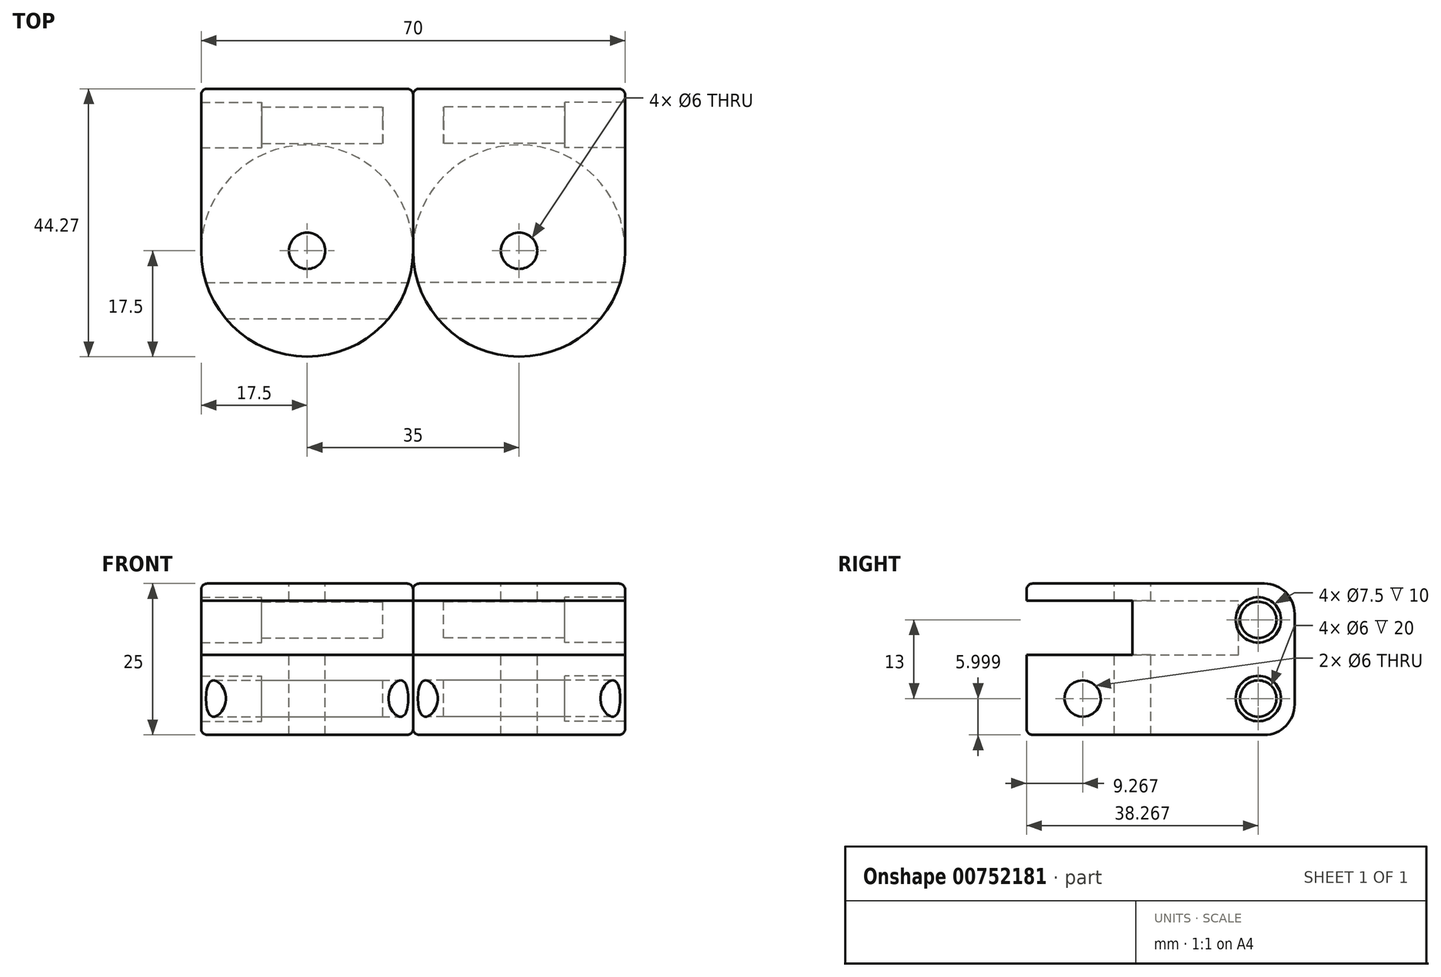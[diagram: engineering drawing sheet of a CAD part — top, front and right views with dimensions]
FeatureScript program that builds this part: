
annotation { "Feature Type Name" : "Feature", "Feature Type Description" : "" }
export const myFeature = defineFeature(function(context is Context, id is Id, definition is map)
    precondition{}
    {
        {
            var Q0;
            Q0=qCreatedBy(makeId("Right.planeOp"),FACE);
            var sketch = newSketch(context, id + "F0", { "sketchPlane" : qUnion([Q0])});
            skLineSegment(sketch, "E0.bottom", {"start": v(-22.23, 10.8) * mm, "end": v(17.77, 10.8) * mm});
            skLineSegment(sketch, "E0.top", {"start": v(-22.23, -14.2) * mm, "end": v(17.77, -14.2) * mm});
            skLineSegment(sketch, "E0.left", {"start": v(-22.23, 10.8) * mm, "end": v(-22.23, -14.2) * mm});
            skLineSegment(sketch, "E0.right", {"start": v(22.77, 5.8) * mm, "end": v(22.77, -9.2) * mm});
            skCircle(sketch, "E1", {"center": v(16.77, 4.8) * mm, "radius": 3 * mm});
            skCircle(sketch, "E2", {"center": v(16.77, -8.2) * mm, "radius": 3 * mm});
            skPoint(sketch, "E3.visualSharp", {"position": v(22.77, 10.8) * mm});
            skArc(sketch, "E3.filletArc", {"start": v(22.77, 5.8) * mm, "mid": v(21.3, 9.33) * mm, "end": v(17.77, 10.8) * mm});
            skPoint(sketch, "E4.visualSharp", {"position": v(22.77, -14.2) * mm});
            skArc(sketch, "E4.filletArc", {"start": v(17.77, -14.2) * mm, "mid": v(21.3, -12.74) * mm, "end": v(22.77, -9.2) * mm});
            skCircle(sketch, "E5", {"center": v(16.77, 4.8) * mm, "radius": 3.75 * mm});
            skCircle(sketch, "E6", {"center": v(16.77, -8.2) * mm, "radius": 3.75 * mm});
            skCircle(sketch, "E7", {"center": v(-12.23, -8.2) * mm, "radius": 3 * mm});
            skSolve(sketch);
        }
        {
            var Q0;
            Q0=makeQuery(id+"F0.imprint","IMPRINT",FACE,{"disambiguationData":[TD([[makeQuery(id+"F0.imprint","IMPRINT",EDGE,{"derivedFrom":sQuery(id+"F0.wireOp",EDGE,"E0.bottom")}),-1.0]])]});
            extrude(context, id + "F1", {"entities" : qUnion([Q0]), "depth" : 35 * mm, "offsetDistance" : 25 * mm});
        }
        {
            var Q0;
            Q0=makeQuery(id+"F0.imprint","IMPRINT",FACE,{"disambiguationData":[TD([[makeQuery(id+"F0.imprint","IMPRINT",EDGE,{"derivedFrom":sQuery(id+"F0.wireOp",EDGE,"E1")}),-1.0]])]});
            var Q1;
            Q1=makeQuery(id+"F0.imprint","IMPRINT",FACE,{"disambiguationData":[TD([[makeQuery(id+"F0.imprint","IMPRINT",EDGE,{"derivedFrom":sQuery(id+"F0.wireOp",EDGE,"E2")}),-1.0]])]});
            extrude(context, id + "F2", {"entities" : qUnion([Q0, Q1]), "operationType" : NewBodyOperationType.ADD, "depth" : 25 * mm, "offsetDistance" : 25 * mm});
        }
        {
            var Q0;
            Q0=makeQuery(id+"F0.imprint","IMPRINT",FACE,{"disambiguationData":[TD([[makeQuery(id+"F0.imprint","IMPRINT",EDGE,{"derivedFrom":sQuery(id+"F0.wireOp",EDGE,"E1")}),1.0]])]});
            var Q1;
            Q1=makeQuery(id+"F0.imprint","IMPRINT",FACE,{"disambiguationData":[TD([[makeQuery(id+"F0.imprint","IMPRINT",EDGE,{"derivedFrom":sQuery(id+"F0.wireOp",EDGE,"E2")}),1.0]])]});
            extrude(context, id + "F3", {"entities" : qUnion([Q0, Q1]), "operationType" : NewBodyOperationType.ADD, "depth" : 5 * mm, "offsetDistance" : 25 * mm});
        }
        {
            var Q0;
            Q0=qCreatedBy(makeId("Top.planeOp"),FACE);
            var sketch = newSketch(context, id + "F4", { "sketchPlane" : qUnion([Q0])});
            skCircle(sketch, "E8", {"center": v(17.5, -4) * mm, "radius": 15 * mm});
            skCircle(sketch, "E9", {"center": v(17.5, -4) * mm, "radius": 17.5 * mm});
            skLineSegment(sketch, "E10", {"start": v(0, 0) * mm, "end": v(0, -24.2) * mm});
            skLineSegment(sketch, "E11", {"start": v(0, -24.2) * mm, "end": v(35, -24.2) * mm});
            skLineSegment(sketch, "E12", {"start": v(35, -24.2) * mm, "end": v(35, 0) * mm});
            skSolve(sketch);
        }
        {
            var Q0;
            {var subQ0=sQuery(id+"F4.wireOp",EDGE,"E10");Q0=makeQuery(id+"F4.imprint","IMPRINT",FACE,{"disambiguationData":[TD([[makeQuery(id+"F4.imprint","IMPRINT",EDGE,{"derivedFrom":subQ0}),1.0]])]});}
            extrude(context, id + "F5", {"entities" : qUnion([Q0]), "operationType" : NewBodyOperationType.REMOVE, "oppositeDirection" : true, "depth" : 25 * mm, "offsetDistance" : 25 * mm, "hasSecondDirection" : true, "secondDirectionOppositeDirection" : false, "secondDirectionDepth" : 25 * mm});
        }
        {
            var Q0;
            Q0=makeQuery(id+"F4.imprint","IMPRINT",FACE,{"disambiguationData":[TD([[makeQuery(id+"F4.imprint","IMPRINT",EDGE,{"derivedFrom":sQuery(id+"F4.wireOp",EDGE,"E8")}),-1.0]])]});
            var Q1;
            Q1=makeQuery(id+"F4.imprint","IMPRINT",FACE,{"disambiguationData":[TD([[makeQuery(id+"F4.imprint","IMPRINT",EDGE,{"derivedFrom":sQuery(id+"F4.wireOp",EDGE,"E8")}),1.0]])]});
            extrude(context, id + "F6", {"entities" : qUnion([Q0, Q1]), "operationType" : NewBodyOperationType.REMOVE, "oppositeDirection" : true, "depth" : 1 * mm, "offsetDistance" : 25 * mm, "hasSecondDirection" : true, "secondDirectionOppositeDirection" : false, "secondDirectionDepth" : 8 * mm});
        }
        {
            var Q0;
            Q0=qCreatedBy(makeId("Top.planeOp"),FACE);
            var sketch = newSketch(context, id + "F7", { "sketchPlane" : qUnion([Q0])});
            skCircle(sketch, "E13", {"center": v(17.5, -4) * mm, "radius": 3 * mm});
            skSolve(sketch);
        }
        {
            var Q0;
            Q0=qSketchRegion(id+"F7",true);
            extrude(context, id + "F8", {"entities" : qUnion([Q0]), "operationType" : NewBodyOperationType.REMOVE, "oppositeDirection" : true, "depth" : 25 * mm, "offsetDistance" : 25 * mm, "hasSecondDirection" : true, "secondDirectionOppositeDirection" : false, "secondDirectionDepth" : 25 * mm});
        }
        {
            var Q0;
            Q0=makeQuery(id+"F5.boolean.opBoolean","INTERSECT",EDGE,{"derivedFrom":[makeQuery(id+"F1.opExtrude","SWEPT_FACE",FACE,{"disambiguationData":[OSD([sQuery(id+"F0.wireOp",EDGE,"E0.top")])]}),makeQuery(id+"F5.opExtrude","SWEPT_FACE",FACE,{"disambiguationData":[OSD([sQuery(id+"F4.wireOp",EDGE,"E9")])]})]});
            var Q1;
            Q1=makeQuery(id+"F1.opExtrude","CAP_EDGE",EDGE,{"disambiguationData":[OSD([sQuery(id+"F0.wireOp",EDGE,"E0.top")])],"isStart":true});
            var Q2;
            Q2=makeQuery(id+"F1.opExtrude","CAP_EDGE",EDGE,{"disambiguationData":[OSD([sQuery(id+"F0.wireOp",EDGE,"E0.top")])],"isStart":false});
            var Q3;
            Q3=makeQuery(id+"F1.opExtrude","CAP_EDGE",EDGE,{"disambiguationData":[OSD([sQuery(id+"F0.wireOp",EDGE,"E4.filletArc")])],"isStart":true});
            var Q4;
            Q4=makeQuery(id+"F1.opExtrude","CAP_EDGE",EDGE,{"disambiguationData":[OSD([sQuery(id+"F0.wireOp",EDGE,"E4.filletArc")])],"isStart":false});
            var Q5;
            Q5=makeQuery(id+"F1.opExtrude","CAP_EDGE",EDGE,{"disambiguationData":[OSD([sQuery(id+"F0.wireOp",EDGE,"E0.right")])],"isStart":false});
            var Q6;
            Q6=makeQuery(id+"F1.opExtrude","CAP_EDGE",EDGE,{"disambiguationData":[OSD([sQuery(id+"F0.wireOp",EDGE,"E3.filletArc")])],"isStart":false});
            var Q7;
            Q7=makeQuery(id+"F1.opExtrude","CAP_EDGE",EDGE,{"disambiguationData":[OSD([sQuery(id+"F0.wireOp",EDGE,"E0.bottom")])],"isStart":false});
            var Q8;
            Q8=makeQuery(id+"F1.opExtrude","CAP_EDGE",EDGE,{"disambiguationData":[OSD([sQuery(id+"F0.wireOp",EDGE,"E0.bottom")])],"isStart":true});
            var Q9;
            Q9=makeQuery(id+"F1.opExtrude","CAP_EDGE",EDGE,{"disambiguationData":[OSD([sQuery(id+"F0.wireOp",EDGE,"E3.filletArc")])],"isStart":true});
            var Q10;
            Q10=makeQuery(id+"F1.opExtrude","CAP_EDGE",EDGE,{"disambiguationData":[OSD([sQuery(id+"F0.wireOp",EDGE,"E0.right")])],"isStart":true});
            fillet(context, id + "F9", {"entities" : qUnion([Q0, Q1, Q2, Q3, Q4, Q5, Q6, Q7, Q8, Q9, Q10]), "radius" : 1 * mm, "tangentPropagation" : true, "allowEdgeOverflow" : false});
        }
        {
            var Q0;
            Q0=makeQuery(id+"F1.opExtrude","SWEPT_BODY",BODY,{"disambiguationData":[OSD([sQuery(id+"F0.wireOp",EDGE,"E0.bottom"),sQuery(id+"F0.wireOp",EDGE,"E0.top"),sQuery(id+"F0.wireOp",EDGE,"E0.left"),sQuery(id+"F0.wireOp",EDGE,"E0.right"),sQuery(id+"F0.wireOp",EDGE,"E3.filletArc"),sQuery(id+"F0.wireOp",EDGE,"E4.filletArc"),sQuery(id+"F0.wireOp",EDGE,"E5"),sQuery(id+"F0.wireOp",EDGE,"E6"),sQuery(id+"F0.wireOp",EDGE,"E7")])]});
            var Q1;
            Q1=qCreatedBy(makeId("Right.planeOp"),FACE);
            mirror(context, id + "F10", {"entities" : qUnion([Q0]), "mirrorPlane" : qUnion([Q1])});
        }
    });
